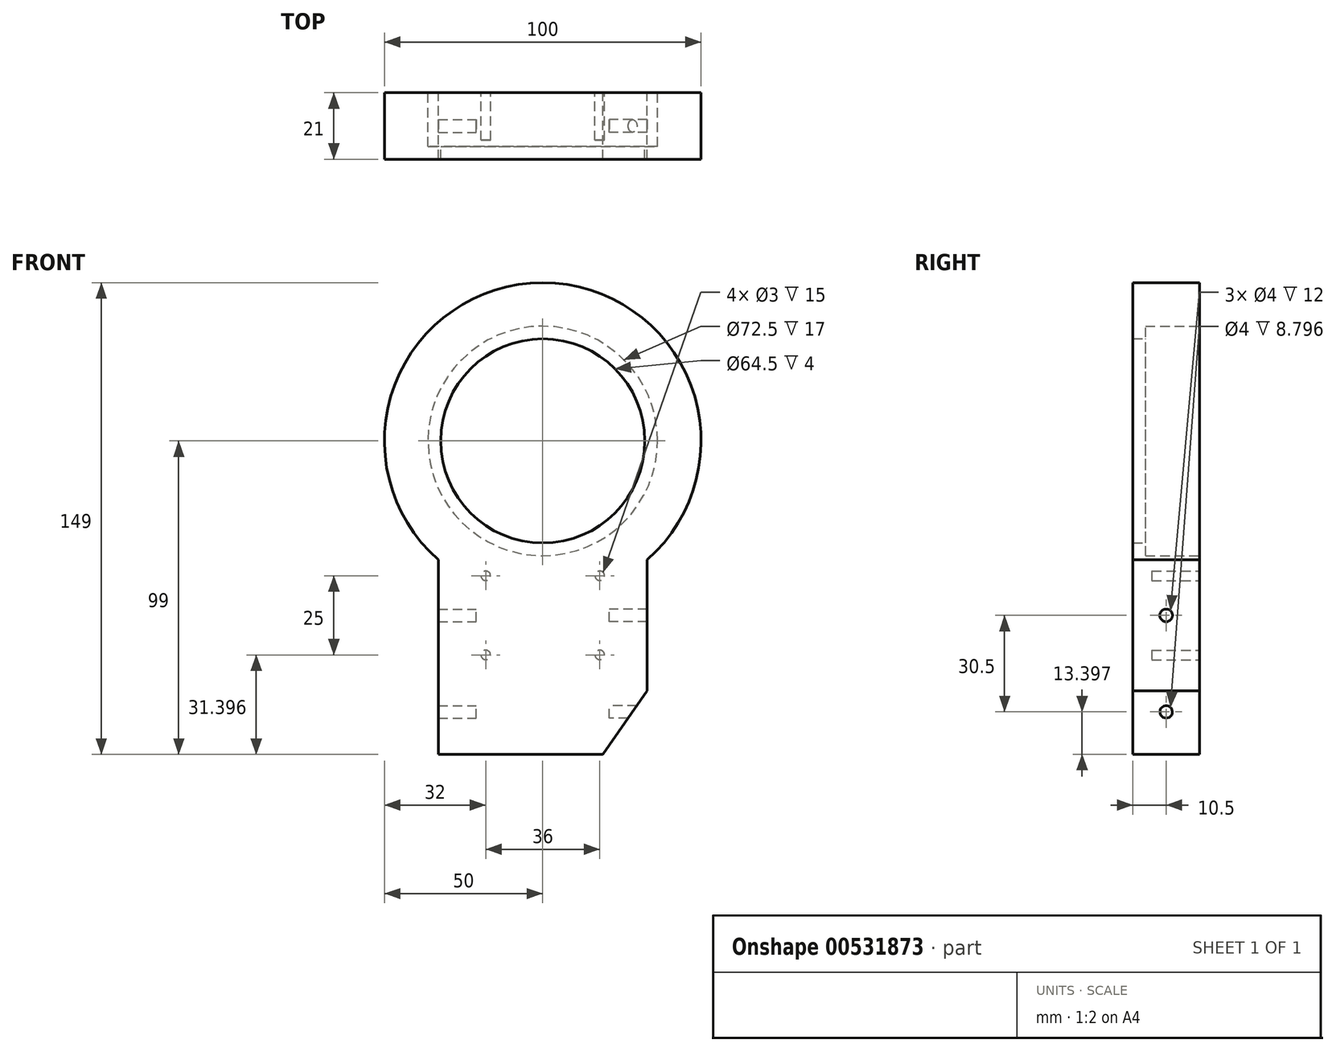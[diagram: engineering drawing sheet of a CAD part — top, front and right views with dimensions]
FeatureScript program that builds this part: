
annotation { "Feature Type Name" : "Feature", "Feature Type Description" : "" }
export const myFeature = defineFeature(function(context is Context, id is Id, definition is map)
    precondition{}
    {
        {
            var Q0;
            Q0=qCreatedBy(makeId("Front.planeOp"),FACE);
            var sketch = newSketch(context, id + "F0", { "sketchPlane" : qUnion([Q0])});
            skCircle(sketch, "E0", {"center": v(0, 0) * mm, "radius": 36.25 * mm});
            skArc(sketch, "E1", {"start": v(50, 0) * mm, "mid": v(0, 50) * mm, "end": v(-50, 0) * mm});
            skPoint(sketch, "E2.endSnap0", {"position": v(0, -99) * mm});
            skLineSegment(sketch, "E3.trimOffspring", {"start": v(-19, -99) * mm, "end": v(19, -99) * mm});
            skArc(sketch, "E4.MirrorCS", {"start": v(50, 0) * mm, "mid": v(45.55, -20.62) * mm, "end": v(33, -37.56) * mm});
            skLineSegment(sketch, "E5.trimOffspring", {"start": v(33, -37.56) * mm, "end": v(33, -79) * mm});
            skLineSegment(sketch, "E6.trimOffspring", {"start": v(-33, -37.56) * mm, "end": v(-33, -79) * mm});
            skArc(sketch, "E7.trimOffspring", {"start": v(-33, -37.56) * mm, "mid": v(-45.55, -20.62) * mm, "end": v(-50, 0) * mm});
            skLineSegment(sketch, "E8", {"start": v(0, -99) * mm, "end": v(0, -81.4) * mm});
            skLineSegment(sketch, "E9.MirrorCS", {"start": v(33, -79) * mm, "end": v(19, -99) * mm});
            skLineSegment(sketch, "E10", {"start": v(-19, -99) * mm, "end": v(-33, -99) * mm});
            skLineSegment(sketch, "E11", {"start": v(-33, -99) * mm, "end": v(-33, -79) * mm});
            skSolve(sketch);
        }
        {
            var Q0;
            Q0=qSketchRegion(id+"F0",true);
            extrude(context, id + "F1", {"entities" : qUnion([Q0]), "depth" : 17 * mm});
        }
        {
            var Q0;
            Q0=makeQuery(id+"F1.opExtrude","CAP_FACE",FACE,{"disambiguationData":[OSD([sQuery(id+"F0.wireOp",EDGE,"E0"),sQuery(id+"F0.wireOp",EDGE,"E1"),sQuery(id+"F0.wireOp",EDGE,"9Qu72541-LivO-jTMm-oUwD-ZALQE2Hvik1n"),sQuery(id+"F0.wireOp",EDGE,"i4TymV6R-teZx-C7h1-2yMt-q0MvK4pHcOex"),sQuery(id+"F0.wireOp",EDGE,"pD05HJNU-Muf5-boTQ-xGwQ-RlADy1BkldT5")])],"isStart":false});
            var sketch = newSketch(context, id + "F2", { "sketchPlane" : qUnion([Q0])});
            skCircle(sketch, "E12", {"center": v(0, 0) * mm, "radius": 32.25 * mm});
            skLineSegment(sketch, "E13.left", {"start": v(33, -37.56) * mm, "end": v(33, -79) * mm});
            skLineSegment(sketch, "E13.right", {"start": v(-33, -37.56) * mm, "end": v(-33, -37.56) * mm});
            skLineSegment(sketch, "E14", {"start": v(-33, -37.56) * mm, "end": v(-33, -99) * mm});
            skLineSegment(sketch, "E15", {"start": v(33, -79) * mm, "end": v(19, -99) * mm});
            skLineSegment(sketch, "E16", {"start": v(-33, -99) * mm, "end": v(19, -99) * mm});
            skArc(sketch, "E17", {"start": v(33, -37.56) * mm, "mid": v(0, 50) * mm, "end": v(-33, -37.56) * mm});
            skSolve(sketch);
        }
        {
            var Q0;
            Q0=qSketchRegion(id+"F2",true);
            extrude(context, id + "F3", {"entities" : qUnion([Q0]), "operationType" : NewBodyOperationType.ADD, "depth" : 4 * mm});
        }
        {
            var Q0;
            Q0=makeQuery(id+"F1.opExtrude","CAP_FACE",FACE,{"disambiguationData":[OSD([sQuery(id+"F0.wireOp",EDGE,"E0"),sQuery(id+"F0.wireOp",EDGE,"E1"),sQuery(id+"F0.wireOp",EDGE,"9Qu72541-LivO-jTMm-oUwD-ZALQE2Hvik1n"),sQuery(id+"F0.wireOp",EDGE,"i4TymV6R-teZx-C7h1-2yMt-q0MvK4pHcOex"),sQuery(id+"F0.wireOp",EDGE,"pD05HJNU-Muf5-boTQ-xGwQ-RlADy1BkldT5")])],"isStart":true});
            var sketch = newSketch(context, id + "F4", { "sketchPlane" : qUnion([Q0])});
            skCircle(sketch, "E18", {"center": v(-18, -42.6) * mm, "radius": 1.5 * mm});
            skCircle(sketch, "E19", {"center": v(18, -42.6) * mm, "radius": 1.5 * mm});
            skCircle(sketch, "E20", {"center": v(18, -67.6) * mm, "radius": 1.5 * mm});
            skCircle(sketch, "E21", {"center": v(-18, -67.6) * mm, "radius": 1.5 * mm});
            skSolve(sketch);
        }
        {
            var Q0;
            Q0=qSketchRegion(id+"F4",true);
            extrude(context, id + "F5", {"entities" : qUnion([Q0]), "operationType" : NewBodyOperationType.REMOVE, "oppositeDirection" : true, "depth" : 15 * mm});
        }
        {
            var Q0;
            Q0=qCreatedBy(makeId("Right.planeOp"),FACE);
            cPlane(context, id + "F6", {"entities" : qUnion([Q0]), "cplaneType" : CPlaneType.OFFSET, "offset" : (33 - 12) * mm, "width" : 150 * mm, "height" : 150 * mm});
        }
        {
            var Q0;
            Q0=qCreatedBy(id+"F6.planeOp",FACE);
            var sketch = newSketch(context, id + "F7", { "sketchPlane" : qUnion([Q0])});
            skLineSegment(sketch, "E22", {"start": v(0, 0) * mm, "end": v(0, -42.6) * mm});
            skLineSegment(sketch, "E23", {"start": v(0, -42.6) * mm, "end": v(0, -67.6) * mm});
            skLineSegment(sketch, "E24", {"start": v(0, -67.6) * mm, "end": v(0, -85.6) * mm});
            skLineSegment(sketch, "E25", {"start": v(0, -55.1) * mm, "end": v(-21, -55.1) * mm});
            skLineSegment(sketch, "E26", {"start": v(0, -85.6) * mm, "end": v(-21, -85.6) * mm});
            skCircle(sketch, "E27", {"center": v(-10.5, -55.1) * mm, "radius": 2 * mm});
            skCircle(sketch, "E28", {"center": v(-10.5, -85.6) * mm, "radius": 2 * mm});
            skSolve(sketch);
        }
        {
            var Q0;
            Q0=qSketchRegion(id+"F7",true);
            extrude(context, id + "F8", {"entities" : qUnion([Q0]), "operationType" : NewBodyOperationType.REMOVE, "depth" : 25 * mm});
        }
        {
            var Q0;
            Q0=qCreatedBy(makeId("Right.planeOp"),FACE);
            cPlane(context, id + "F9", {"entities" : qUnion([Q0]), "cplaneType" : CPlaneType.OFFSET, "offset" : (33 - 12) * mm, "oppositeDirection" : true, "width" : 150 * mm, "height" : 150 * mm});
        }
        {
            var Q0;
            Q0=qCreatedBy(id+"F9.planeOp",FACE);
            var sketch = newSketch(context, id + "F10", { "sketchPlane" : qUnion([Q0])});
            skLineSegment(sketch, "E29", {"start": v(0, 0) * mm, "end": v(0, -42.6) * mm});
            skLineSegment(sketch, "E30", {"start": v(0, -42.6) * mm, "end": v(0, -67.6) * mm});
            skLineSegment(sketch, "E31", {"start": v(0, -67.6) * mm, "end": v(0, -85.6) * mm});
            skLineSegment(sketch, "E32", {"start": v(0, -85.6) * mm, "end": v(-21, -85.6) * mm});
            skLineSegment(sketch, "E33", {"start": v(0, -55.1) * mm, "end": v(-21, -55.1) * mm});
            skCircle(sketch, "E34", {"center": v(-10.5, -55.1) * mm, "radius": 2 * mm});
            skCircle(sketch, "E35", {"center": v(-10.5, -85.6) * mm, "radius": 2 * mm});
            skSolve(sketch);
        }
        {
            var Q0;
            Q0=qSketchRegion(id+"F10",true);
            extrude(context, id + "F11", {"entities" : qUnion([Q0]), "operationType" : NewBodyOperationType.REMOVE, "oppositeDirection" : true, "depth" : 25 * mm});
        }
    });
